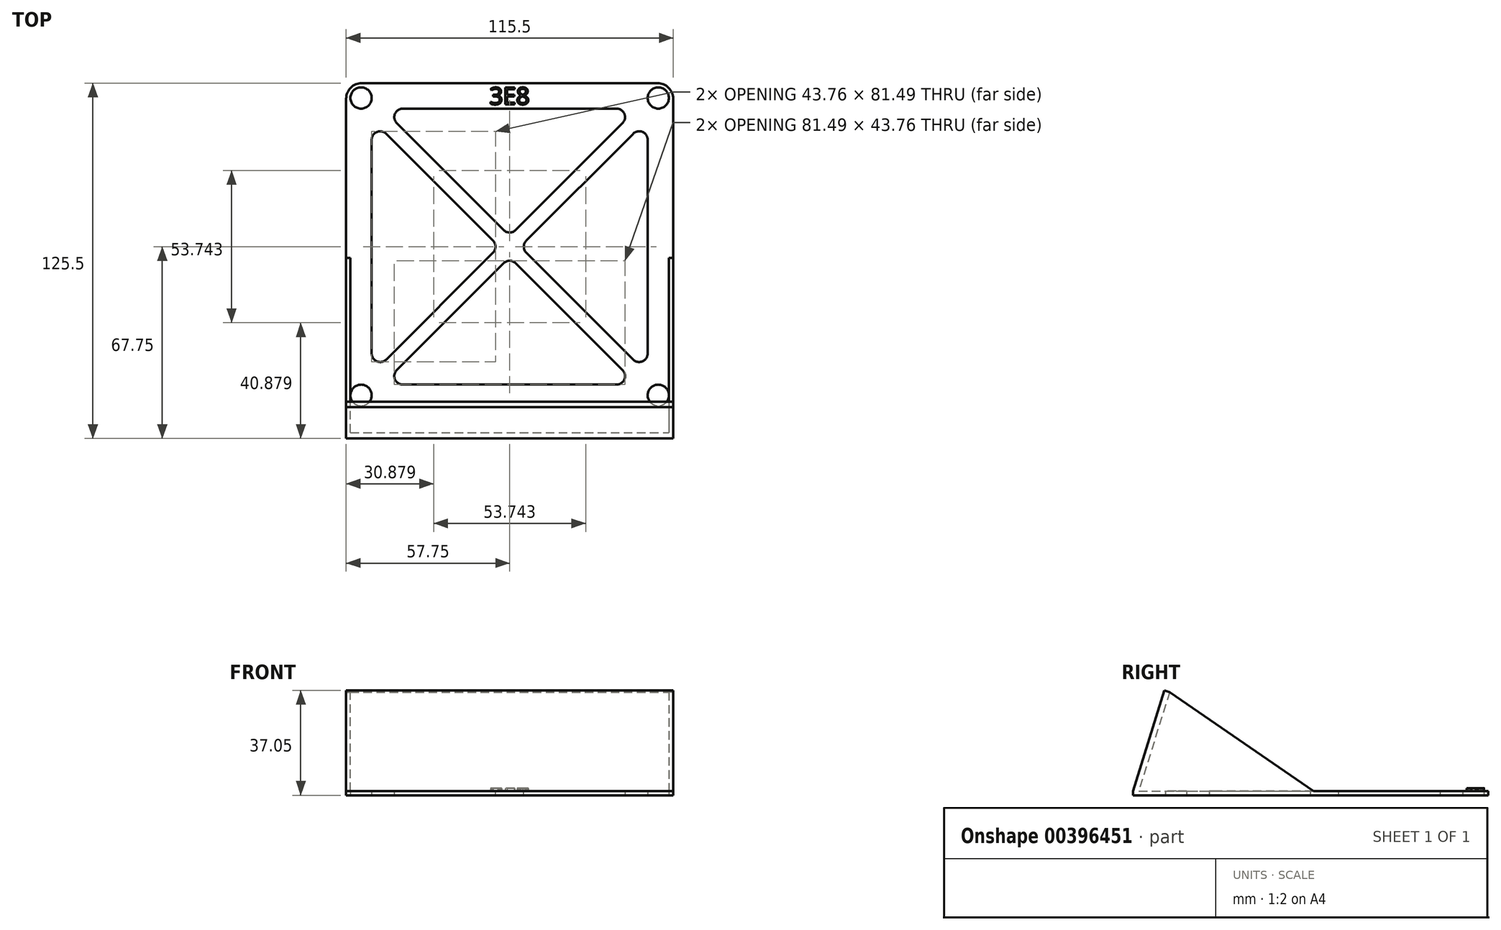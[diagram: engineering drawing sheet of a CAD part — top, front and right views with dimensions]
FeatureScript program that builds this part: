
annotation { "Feature Type Name" : "Feature", "Feature Type Description" : "" }
export const myFeature = defineFeature(function(context is Context, id is Id, definition is map)
    precondition{}
    {
        {
            assignVariable(context, id + "F0", {"name" : "HoleDiam", "anyValue" : 7.5});
        }
        {
            var Q0;
            Q0=qCreatedBy(makeId("Top.planeOp"),FACE);
            var sketch = newSketch(context, id + "F1", { "sketchPlane" : qUnion([Q0])});
            skLineSegment(sketch, "E0.bottom", {"start": v(52.5, -52.5) * mm, "end": v(-52.5, -52.5) * mm, "construction": true});
            skLineSegment(sketch, "E0.top", {"start": v(52.5, 52.5) * mm, "end": v(-52.5, 52.5) * mm, "construction": true});
            skLineSegment(sketch, "E0.left", {"start": v(52.5, -52.5) * mm, "end": v(52.5, 52.5) * mm, "construction": true});
            skLineSegment(sketch, "E0.right", {"start": v(-52.5, -52.5) * mm, "end": v(-52.5, 52.5) * mm, "construction": true});
            skPoint(sketch, "E0.middle", {"position": v(0, 0) * mm});
            skCircle(sketch, "E1", {"center": v(-52.5, 52.5) * mm, "radius": 3.75 * mm});
            skCircle(sketch, "E2", {"center": v(52.5, 52.5) * mm, "radius": 3.75 * mm});
            skCircle(sketch, "E3", {"center": v(52.5, -52.5) * mm, "radius": 3.75 * mm});
            skCircle(sketch, "E4", {"center": v(-52.5, -52.5) * mm, "radius": 3.75 * mm});
            skLineSegment(sketch, "E5.bottom", {"start": v(57.75, 57.75) * mm, "end": v(-57.75, 57.75) * mm});
            skLineSegment(sketch, "E5.top", {"start": v(57.75, -57.75) * mm, "end": v(-57.75, -57.75) * mm});
            skLineSegment(sketch, "E5.left", {"start": v(57.75, 57.75) * mm, "end": v(57.75, -57.75) * mm});
            skLineSegment(sketch, "E5.right", {"start": v(-57.75, 57.75) * mm, "end": v(-57.75, -57.75) * mm});
            skPoint(sketch, "E6.endSnap0", {"position": v(0, 52.5) * mm});
            skLineSegment(sketch, "E7", {"start": v(0, 52.5) * mm, "end": v(0, 48.75) * mm, "construction": true});
            skLineSegment(sketch, "E8", {"start": v(-45, 48.75) * mm, "end": v(45, 48.75) * mm});
            skLineSegment(sketch, "E9", {"start": v(-45, 48.75) * mm, "end": v(0, 3.75) * mm});
            skLineSegment(sketch, "E10", {"start": v(0, 3.75) * mm, "end": v(45, 48.75) * mm});
            skLineSegment(sketch, "E11.1.0", {"start": v(-48.75, -45) * mm, "end": v(-3.75, 0) * mm});
            skLineSegment(sketch, "E11.1.1", {"start": v(-48.75, -45) * mm, "end": v(-48.75, 45) * mm});
            skLineSegment(sketch, "E11.1.2", {"start": v(-3.75, 0) * mm, "end": v(-48.75, 45) * mm});
            skLineSegment(sketch, "E11.2.0", {"start": v(45, -48.75) * mm, "end": v(0, -3.75) * mm});
            skLineSegment(sketch, "E11.2.1", {"start": v(45, -48.75) * mm, "end": v(-45, -48.75) * mm});
            skLineSegment(sketch, "E11.2.2", {"start": v(0, -3.75) * mm, "end": v(-45, -48.75) * mm});
            skLineSegment(sketch, "E11.3.0", {"start": v(48.75, 45) * mm, "end": v(3.75, 0) * mm});
            skLineSegment(sketch, "E11.3.1", {"start": v(48.75, 45) * mm, "end": v(48.75, -45) * mm});
            skLineSegment(sketch, "E11.3.2", {"start": v(3.75, 0) * mm, "end": v(48.75, -45) * mm});
            skSolve(sketch);
        }
        {
            var Q0;
            Q0 = qSketchRegion(id + "F1", true);
            extrude(context, id + "F2", {"entities" : qUnion([Q0]), "depth" : 1.5 * mm});
        }
        {
            var Q0;
            Q0=makeQuery(id+"F2.opExtrude","SWEPT_FACE",FACE,{"disambiguationData":[OSD([sQuery(id+"F1.wireOp",EDGE,"E5.top")])]});
            extrude(context, id + "F3", {"entities" : qUnion([Q0]), "operationType" : NewBodyOperationType.ADD, "depth" : 10 * mm});
        }
        {
            var Q0;
            {var subQ0=sQuery(id+"F1.wireOp",EDGE,"E5.left");Q0=makeQuery(id+"F3.boolean.opBoolean","MERGE",FACE,{"derivedFrom":[makeQuery(id+"F2.opExtrude","SWEPT_FACE",FACE,{"disambiguationData":[OSD([subQ0])]}),makeQuery(id+"F3.opExtrude","SWEPT_FACE",FACE,{"disambiguationData":[OSD([sQuery(id+"F1.wireOp",EDGE,"E5.top"),subQ0])]})]});}
            var sketch = newSketch(context, id + "F4", { "sketchPlane" : qUnion([Q0])});
            skLineSegment(sketch, "E12", {"start": v(-67.75, 1.5) * mm, "end": v(-56.71, 37.05) * mm});
            skLineSegment(sketch, "E13", {"start": v(-56.71, 37.05) * mm, "end": v(-54.8, 36.45) * mm});
            skLineSegment(sketch, "E14", {"start": v(-54.8, 36.45) * mm, "end": v(-65.66, 1.5) * mm});
            skLineSegment(sketch, "E15", {"start": v(-65.66, 1.5) * mm, "end": v(-67.75, 1.5) * mm});
            skLineSegment(sketch, "E16", {"start": v(-54.8, 36.45) * mm, "end": v(57.75, 1.5) * mm, "construction": true});
            skSolve(sketch);
        }
        {
            var Q0;
            Q0 = qSketchRegion(id + "F4", true);
            var Q1;
            {var subQ0=sQuery(id+"F1.wireOp",EDGE,"E5.right");Q1=makeQuery(id+"F3.boolean.opBoolean","MERGE",FACE,{"derivedFrom":[makeQuery(id+"F2.opExtrude","SWEPT_FACE",FACE,{"disambiguationData":[OSD([subQ0])]}),makeQuery(id+"F3.opExtrude","SWEPT_FACE",FACE,{"disambiguationData":[OSD([sQuery(id+"F1.wireOp",EDGE,"E5.top"),subQ0])]})]});}
            extrude(context, id + "F5", {"entities" : qUnion([Q0]), "operationType" : NewBodyOperationType.ADD, "endBound" : BoundingType.UP_TO_SURFACE, "oppositeDirection" : true, "endBoundEntityFace" : qUnion([Q1]), "depth" : 25 * mm});
        }
        {
            var Q0;
            {var subQ0=sQuery(id+"F1.wireOp",EDGE,"E5.top");Q0=makeQuery(id+"F3.boolean.opBoolean","MERGE",FACE,{"derivedFrom":[makeQuery(id+"F2.opExtrude","CAP_FACE",FACE,{"disambiguationData":[OSD([sQuery(id+"F1.wireOp",EDGE,"E1"),sQuery(id+"F1.wireOp",EDGE,"E2"),sQuery(id+"F1.wireOp",EDGE,"E3"),sQuery(id+"F1.wireOp",EDGE,"E4"),sQuery(id+"F1.wireOp",EDGE,"E5.bottom"),subQ0,sQuery(id+"F1.wireOp",EDGE,"E5.left"),sQuery(id+"F1.wireOp",EDGE,"E5.right"),sQuery(id+"F1.wireOp",EDGE,"E8"),sQuery(id+"F1.wireOp",EDGE,"E9"),sQuery(id+"F1.wireOp",EDGE,"E10"),sQuery(id+"F1.wireOp",EDGE,"E11.1.0"),sQuery(id+"F1.wireOp",EDGE,"E11.1.1"),sQuery(id+"F1.wireOp",EDGE,"E11.1.2"),sQuery(id+"F1.wireOp",EDGE,"E11.2.0"),sQuery(id+"F1.wireOp",EDGE,"E11.2.1"),sQuery(id+"F1.wireOp",EDGE,"E11.2.2"),sQuery(id+"F1.wireOp",EDGE,"E11.3.0"),sQuery(id+"F1.wireOp",EDGE,"E11.3.1"),sQuery(id+"F1.wireOp",EDGE,"E11.3.2")])],"isStart":false}),makeQuery(id+"F3.opExtrude","SWEPT_FACE",FACE,{"disambiguationData":[OSD([subQ0]),TDD([makeQuery(id+"F2.opExtrude","CAP_EDGE",EDGE,{"disambiguationData":[OSD([subQ0])],"isStart":false})])]})]});}
            var sketch = newSketch(context, id + "F6", { "sketchPlane" : qUnion([Q0])});
            skPoint(sketch, "E17.0", {"position": v(-57.75, -65.66) * mm});
            skPoint(sketch, "E18.oppositeSnap0", {"position": v(-57.75, -3.95) * mm});
            skLineSegment(sketch, "E18.bottom", {"start": v(-57.75, -65.66) * mm, "end": v(-56.25, -65.66) * mm});
            skLineSegment(sketch, "E18.top", {"start": v(-57.75, -3.95) * mm, "end": v(-56.25, -3.95) * mm});
            skLineSegment(sketch, "E18.left", {"start": v(-57.75, -65.66) * mm, "end": v(-57.75, -3.95) * mm});
            skLineSegment(sketch, "E18.right", {"start": v(-56.25, -65.66) * mm, "end": v(-56.25, -3.95) * mm});
            skLineSegment(sketch, "E19", {"start": v(0, 0) * mm, "end": v(0, -48.75) * mm, "construction": true});
            skLineSegment(sketch, "E20.MirrorCS", {"start": v(56.25, -65.66) * mm, "end": v(56.25, -3.95) * mm});
            skLineSegment(sketch, "E21.MirrorCS", {"start": v(57.75, -3.95) * mm, "end": v(56.25, -3.95) * mm});
            skLineSegment(sketch, "E22.MirrorCS", {"start": v(57.75, -65.66) * mm, "end": v(57.75, -3.95) * mm});
            skLineSegment(sketch, "E23.MirrorCS", {"start": v(57.75, -65.66) * mm, "end": v(56.25, -65.66) * mm});
            skSolve(sketch);
        }
        {
            var Q0;
            Q0=makeQuery(id+"F5.opExtrude","SWEPT_FACE",FACE,{"disambiguationData":[OSD([sQuery(id+"F4.wireOp",EDGE,"E14")])]});
            var sketch = newSketch(context, id + "F7", { "sketchPlane" : qUnion([Q0])});
            skLineSegment(sketch, "E24", {"start": v(0, -18.04) * mm, "end": v(0, 18.56) * mm, "construction": true});
            skLineSegment(sketch, "E25.MirrorCS", {"start": v(-56.25, -18.04) * mm, "end": v(-56.25, 18.56) * mm});
            skLineSegment(sketch, "E26.MirrorCS", {"start": v(-57.75, 18.56) * mm, "end": v(-56.25, 18.56) * mm});
            skLineSegment(sketch, "E27.MirrorCS", {"start": v(-57.75, -18.04) * mm, "end": v(-57.75, 18.56) * mm});
            skLineSegment(sketch, "E28.MirrorCS", {"start": v(-57.75, -18.04) * mm, "end": v(-56.25, -18.04) * mm});
            skLineSegment(sketch, "E29.0", {"start": v(-57.75, -18.04) * mm, "end": v(-56.25, -18.04) * mm, "construction": true});
            skLineSegment(sketch, "E30.MirrorCS", {"start": v(56.25, -18.04) * mm, "end": v(56.25, 18.56) * mm});
            skLineSegment(sketch, "E31.MirrorCS", {"start": v(57.75, -18.04) * mm, "end": v(57.75, 18.56) * mm});
            skLineSegment(sketch, "E32.MirrorCS", {"start": v(57.75, -18.04) * mm, "end": v(56.25, -18.04) * mm});
            skLineSegment(sketch, "E33.MirrorCS", {"start": v(57.75, 18.56) * mm, "end": v(56.25, 18.56) * mm});
            skSolve(sketch);
        }
        {
            var Q0;
            Q0=sQuery(id+"F6.wireOp",VERTEX,"E18.right.end");
            var Q1;
            Q1=sQuery(id+"F7.wireOp",VERTEX,"E33.MirrorCS.start");
            var Q2;
            Q2=sQuery(id+"F6.wireOp",VERTEX,"E18.oppositeSnap0");
            cPlane(context, id + "F8", {"entities" : qUnion([Q0, Q1, Q2]), "cplaneType" : CPlaneType.THREE_POINT, "offset" : 25 * mm, "width" : 150 * mm, "height" : 150 * mm});
        }
        {
            var Q0;
            Q0=qCreatedBy(id+"F8.planeOp",FACE);
            var sketch = newSketch(context, id + "F9", { "sketchPlane" : qUnion([Q0])});
            skLineSegment(sketch, "E34.0", {"start": v(-57.75, -4.1) * mm, "end": v(-56.25, -4.1) * mm});
            skLineSegment(sketch, "E35.0", {"start": v(-57.75, -54.95) * mm, "end": v(-57.75, -4.1) * mm});
            skLineSegment(sketch, "E36.0", {"start": v(-56.25, -54.95) * mm, "end": v(-56.25, -4.1) * mm});
            skLineSegment(sketch, "E37.0", {"start": v(-57.75, -54.95) * mm, "end": v(-57.75, -65.81) * mm});
            skLineSegment(sketch, "E38.0", {"start": v(-56.25, -54.95) * mm, "end": v(-56.25, -65.81) * mm});
            skLineSegment(sketch, "E39.0", {"start": v(-57.75, -65.81) * mm, "end": v(-56.25, -65.81) * mm});
            skLineSegment(sketch, "E40.0", {"start": v(0, -0.85) * mm, "end": v(0, -41.02) * mm, "construction": true});
            skLineSegment(sketch, "E41.MirrorCS", {"start": v(57.75, -54.95) * mm, "end": v(57.75, -4.1) * mm});
            skLineSegment(sketch, "E42.MirrorCS", {"start": v(57.75, -4.1) * mm, "end": v(56.25, -4.1) * mm});
            skLineSegment(sketch, "E43.MirrorCS", {"start": v(56.25, -54.95) * mm, "end": v(56.25, -4.1) * mm});
            skLineSegment(sketch, "E44.MirrorCS", {"start": v(57.75, -54.95) * mm, "end": v(57.75, -65.81) * mm});
            skLineSegment(sketch, "E45.MirrorCS", {"start": v(56.25, -54.95) * mm, "end": v(56.25, -65.81) * mm});
            skLineSegment(sketch, "E46.MirrorCS", {"start": v(57.75, -65.81) * mm, "end": v(56.25, -65.81) * mm});
            skSolve(sketch);
        }
        {
            var Q0;
            Q0 = qSketchRegion(id + "F9", true);
            var Q1;
            Q1=makeQuery(id+"F2.opExtrude","SWEPT_BODY",BODY,{"disambiguationData":[OSD([sQuery(id+"F1.wireOp",EDGE,"E1"),sQuery(id+"F1.wireOp",EDGE,"E2"),sQuery(id+"F1.wireOp",EDGE,"E3"),sQuery(id+"F1.wireOp",EDGE,"E4"),sQuery(id+"F1.wireOp",EDGE,"E5.bottom"),sQuery(id+"F1.wireOp",EDGE,"E5.top"),sQuery(id+"F1.wireOp",EDGE,"E5.left"),sQuery(id+"F1.wireOp",EDGE,"E5.right"),sQuery(id+"F1.wireOp",EDGE,"E8"),sQuery(id+"F1.wireOp",EDGE,"E9"),sQuery(id+"F1.wireOp",EDGE,"E10"),sQuery(id+"F1.wireOp",EDGE,"E11.1.0"),sQuery(id+"F1.wireOp",EDGE,"E11.1.1"),sQuery(id+"F1.wireOp",EDGE,"E11.1.2"),sQuery(id+"F1.wireOp",EDGE,"E11.2.0"),sQuery(id+"F1.wireOp",EDGE,"E11.2.1"),sQuery(id+"F1.wireOp",EDGE,"E11.2.2"),sQuery(id+"F1.wireOp",EDGE,"E11.3.0"),sQuery(id+"F1.wireOp",EDGE,"E11.3.1"),sQuery(id+"F1.wireOp",EDGE,"E11.3.2")])]});
            extrude(context, id + "F10", {"entities" : qUnion([Q0]), "operationType" : NewBodyOperationType.ADD, "endBound" : BoundingType.UP_TO_BODY, "oppositeDirection" : true, "endBoundEntityBody" : qUnion([Q1]), "depth" : 25 * mm});
        }
        {
            var Q0;
            Q0=makeQuery(id+"F2.opExtrude","SWEPT_EDGE",EDGE,{"disambiguationData":[OSD([sQuery(id+"F1.wireOp",EDGE,"E11.2.0"),sQuery(id+"F1.wireOp",EDGE,"E11.2.2")])]});
            var Q1;
            Q1=makeQuery(id+"F2.opExtrude","SWEPT_EDGE",EDGE,{"disambiguationData":[OSD([sQuery(id+"F1.wireOp",EDGE,"E11.3.0"),sQuery(id+"F1.wireOp",EDGE,"E11.3.2")])]});
            var Q2;
            Q2=makeQuery(id+"F2.opExtrude","SWEPT_EDGE",EDGE,{"disambiguationData":[OSD([sQuery(id+"F1.wireOp",EDGE,"E9"),sQuery(id+"F1.wireOp",EDGE,"E10")])]});
            var Q3;
            Q3=makeQuery(id+"F2.opExtrude","SWEPT_EDGE",EDGE,{"disambiguationData":[OSD([sQuery(id+"F1.wireOp",EDGE,"E11.1.0"),sQuery(id+"F1.wireOp",EDGE,"E11.1.2")])]});
            var Q4;
            Q4=makeQuery(id+"F2.opExtrude","SWEPT_EDGE",EDGE,{"disambiguationData":[OSD([sQuery(id+"F1.wireOp",EDGE,"E11.2.0"),sQuery(id+"F1.wireOp",EDGE,"E11.2.1")])]});
            var Q5;
            Q5=makeQuery(id+"F2.opExtrude","SWEPT_EDGE",EDGE,{"disambiguationData":[OSD([sQuery(id+"F1.wireOp",EDGE,"E11.3.1"),sQuery(id+"F1.wireOp",EDGE,"E11.3.2")])]});
            var Q6;
            Q6=makeQuery(id+"F2.opExtrude","SWEPT_EDGE",EDGE,{"disambiguationData":[OSD([sQuery(id+"F1.wireOp",EDGE,"E11.2.1"),sQuery(id+"F1.wireOp",EDGE,"E11.2.2")])]});
            var Q7;
            Q7=makeQuery(id+"F2.opExtrude","SWEPT_EDGE",EDGE,{"disambiguationData":[OSD([sQuery(id+"F1.wireOp",EDGE,"E11.1.0"),sQuery(id+"F1.wireOp",EDGE,"E11.1.1")])]});
            var Q8;
            Q8=makeQuery(id+"F2.opExtrude","SWEPT_EDGE",EDGE,{"disambiguationData":[OSD([sQuery(id+"F1.wireOp",EDGE,"E11.1.1"),sQuery(id+"F1.wireOp",EDGE,"E11.1.2")])]});
            var Q9;
            Q9=makeQuery(id+"F2.opExtrude","SWEPT_EDGE",EDGE,{"disambiguationData":[OSD([sQuery(id+"F1.wireOp",EDGE,"E8"),sQuery(id+"F1.wireOp",EDGE,"E9")])]});
            var Q10;
            Q10=makeQuery(id+"F2.opExtrude","SWEPT_EDGE",EDGE,{"disambiguationData":[OSD([sQuery(id+"F1.wireOp",EDGE,"E8"),sQuery(id+"F1.wireOp",EDGE,"E10")])]});
            var Q11;
            Q11=makeQuery(id+"F2.opExtrude","SWEPT_EDGE",EDGE,{"disambiguationData":[OSD([sQuery(id+"F1.wireOp",EDGE,"E11.3.0"),sQuery(id+"F1.wireOp",EDGE,"E11.3.1")])]});
            var Q12;
            {var subQ0=sQuery(id+"F9.wireOp",EDGE,"E39.0");var subQ1=sQuery(id+"F9.wireOp",EDGE,"E38.0");var subQ2=sQuery(id+"F9.wireOp",EDGE,"E37.0");var subQ3=sQuery(id+"F9.wireOp",EDGE,"E36.0");var subQ4=sQuery(id+"F9.wireOp",EDGE,"E35.0");var subQ5=sQuery(id+"F9.wireOp",EDGE,"E34.0");var subQ6=sQuery(id+"F1.wireOp",EDGE,"E5.top");var subQ7=makeQuery(id+"F3.opExtrude","SWEPT_FACE",FACE,{"disambiguationData":[OSD([subQ6]),TDD([makeQuery(id+"F2.opExtrude","CAP_EDGE",EDGE,{"disambiguationData":[OSD([subQ6])],"isStart":false})])]});var subQ8=sQuery(id+"F1.wireOp",EDGE,"E4");var subQ10=makeQuery(id+"F2.opExtrude","CAP_FACE",FACE,{"disambiguationData":[OSD([sQuery(id+"F1.wireOp",EDGE,"E1"),sQuery(id+"F1.wireOp",EDGE,"E2"),sQuery(id+"F1.wireOp",EDGE,"E3"),subQ8,sQuery(id+"F1.wireOp",EDGE,"E5.bottom"),subQ6,sQuery(id+"F1.wireOp",EDGE,"E5.left"),sQuery(id+"F1.wireOp",EDGE,"E5.right"),sQuery(id+"F1.wireOp",EDGE,"E8"),sQuery(id+"F1.wireOp",EDGE,"E9"),sQuery(id+"F1.wireOp",EDGE,"E10"),sQuery(id+"F1.wireOp",EDGE,"E11.1.0"),sQuery(id+"F1.wireOp",EDGE,"E11.1.1"),sQuery(id+"F1.wireOp",EDGE,"E11.1.2"),sQuery(id+"F1.wireOp",EDGE,"E11.2.0"),sQuery(id+"F1.wireOp",EDGE,"E11.2.1"),sQuery(id+"F1.wireOp",EDGE,"E11.2.2"),sQuery(id+"F1.wireOp",EDGE,"E11.3.0"),sQuery(id+"F1.wireOp",EDGE,"E11.3.1"),sQuery(id+"F1.wireOp",EDGE,"E11.3.2")])],"isStart":false});var subQ12=makeQuery(id+"F10.opExtrude","CAP_EDGE",EDGE,{"disambiguationData":[OSD([subQ3,subQ1])],"isStart":false});Q12=qUnion([makeQuery(id+"F10.boolean.opBoolean","SPLIT",EDGE,{"disambiguationData":[TD([makeQuery(id+"F5.opExtrude","SWEPT_FACE",FACE,{"disambiguationData":[OSD([sQuery(id+"F4.wireOp",EDGE,"E14")])]})])],"derivedFrom":subQ12}),makeQuery(id+"F10.opExtrude","TWEAK_EDGE",EDGE,{"derivedFrom":[makeQuery(id+"F3.boolean.opBoolean","MERGE",FACE,{"derivedFrom":[subQ10,subQ7]}),makeQuery(id+"F9.imprint","IMPRINT",EDGE,{"derivedFrom":subQ5}),makeQuery(id+"F9.imprint","IMPRINT",EDGE,{"derivedFrom":subQ4}),makeQuery(id+"F9.imprint","IMPRINT",EDGE,{"derivedFrom":subQ3}),makeQuery(id+"F9.imprint","IMPRINT",EDGE,{"derivedFrom":subQ2}),makeQuery(id+"F9.imprint","IMPRINT",EDGE,{"derivedFrom":subQ1}),makeQuery(id+"F9.imprint","IMPRINT",EDGE,{"derivedFrom":subQ0})]}),makeQuery(id+"F10.boolean.opBoolean","SPLIT",EDGE,{"disambiguationData":[TD([makeQuery(id+"F10.opExtrude","CAP_FACE",FACE,{"disambiguationData":[OSD([subQ5,subQ4,subQ3,subQ2,subQ1,subQ0])],"isStart":true})])],"derivedFrom":subQ12})]);}
            var Q13;
            Q13=makeQuery(id+"F10.opExtrude","TWEAK_EDGE",EDGE,{"derivedFrom":[makeQuery(id+"F5.opExtrude","SWEPT_FACE",FACE,{"disambiguationData":[OSD([sQuery(id+"F4.wireOp",EDGE,"E14")])]}),makeQuery(id+"F9.imprint","IMPRINT",EDGE,{"derivedFrom":sQuery(id+"F9.wireOp",EDGE,"E36.0")}),makeQuery(id+"F9.imprint","IMPRINT",EDGE,{"derivedFrom":sQuery(id+"F9.wireOp",EDGE,"E38.0")})]});
            var Q14;
            Q14=makeQuery(id+"F5.opExtrude","SWEPT_EDGE",EDGE,{"disambiguationData":[OSD([sQuery(id+"F1.wireOp",EDGE,"E5.top"),sQuery(id+"F1.wireOp",EDGE,"E5.left"),sQuery(id+"F4.wireOp",EDGE,"E14"),sQuery(id+"F4.wireOp",EDGE,"E15")])]});
            var Q15;
            Q15=makeQuery(id+"F10.opExtrude","CAP_EDGE",EDGE,{"disambiguationData":[OSD([sQuery(id+"F9.wireOp",EDGE,"E42.MirrorCS")])],"isStart":false});
            var Q16;
            {var subQ0=sQuery(id+"F1.wireOp",EDGE,"E5.top");var subQ1=makeQuery(id+"F3.opExtrude","SWEPT_FACE",FACE,{"disambiguationData":[OSD([subQ0]),TDD([makeQuery(id+"F2.opExtrude","CAP_EDGE",EDGE,{"disambiguationData":[OSD([subQ0])],"isStart":false})])]});var subQ2=sQuery(id+"F1.wireOp",EDGE,"E3");var subQ3=sQuery(id+"F9.wireOp",EDGE,"E45.MirrorCS");var subQ4=sQuery(id+"F9.wireOp",EDGE,"E43.MirrorCS");var subQ5=makeQuery(id+"F2.opExtrude","CAP_FACE",FACE,{"disambiguationData":[OSD([sQuery(id+"F1.wireOp",EDGE,"E1"),sQuery(id+"F1.wireOp",EDGE,"E2"),subQ2,sQuery(id+"F1.wireOp",EDGE,"E4"),sQuery(id+"F1.wireOp",EDGE,"E5.bottom"),subQ0,sQuery(id+"F1.wireOp",EDGE,"E5.left"),sQuery(id+"F1.wireOp",EDGE,"E5.right"),sQuery(id+"F1.wireOp",EDGE,"E8"),sQuery(id+"F1.wireOp",EDGE,"E9"),sQuery(id+"F1.wireOp",EDGE,"E10"),sQuery(id+"F1.wireOp",EDGE,"E11.1.0"),sQuery(id+"F1.wireOp",EDGE,"E11.1.1"),sQuery(id+"F1.wireOp",EDGE,"E11.1.2"),sQuery(id+"F1.wireOp",EDGE,"E11.2.0"),sQuery(id+"F1.wireOp",EDGE,"E11.2.1"),sQuery(id+"F1.wireOp",EDGE,"E11.2.2"),sQuery(id+"F1.wireOp",EDGE,"E11.3.0"),sQuery(id+"F1.wireOp",EDGE,"E11.3.1"),sQuery(id+"F1.wireOp",EDGE,"E11.3.2")])],"isStart":false});Q16=makeQuery(id+"F10.boolean.opBoolean","SPLIT",EDGE,{"disambiguationData":[TD([makeQuery(id+"F10.opExtrude","CAP_FACE",FACE,{"disambiguationData":[OSD([sQuery(id+"F9.wireOp",EDGE,"E41.MirrorCS"),sQuery(id+"F9.wireOp",EDGE,"E42.MirrorCS"),subQ4,sQuery(id+"F9.wireOp",EDGE,"E44.MirrorCS"),subQ3,sQuery(id+"F9.wireOp",EDGE,"E46.MirrorCS")])],"isStart":true})])],"derivedFrom":makeQuery(id+"F10.opExtrude","TWEAK_EDGE",EDGE,{"derivedFrom":[makeQuery(id+"F3.boolean.opBoolean","MERGE",FACE,{"derivedFrom":[subQ5,subQ1]}),makeQuery(id+"F9.imprint","IMPRINT",EDGE,{"derivedFrom":subQ4}),makeQuery(id+"F9.imprint","IMPRINT",EDGE,{"derivedFrom":subQ3})]})});}
            var Q17;
            Q17=makeQuery(id+"F10.opExtrude","CAP_EDGE",EDGE,{"disambiguationData":[OSD([sQuery(id+"F9.wireOp",EDGE,"E43.MirrorCS"),sQuery(id+"F9.wireOp",EDGE,"E45.MirrorCS")])],"isStart":false});
            fillet(context, id + "F11", {"entities" : qUnion([Q0, Q1, Q2, Q3, Q4, Q5, Q6, Q7, Q8, Q9, Q10, Q11, Q12, Q13, Q14, Q15, Q16, Q17]), "radius" : 3 * mm, "tangentPropagation" : true, "allowEdgeOverflow" : false});
        }
        {
            var Q0;
            Q0=makeQuery(id+"F2.opExtrude","SWEPT_EDGE",EDGE,{"disambiguationData":[OSD([sQuery(id+"F1.wireOp",EDGE,"E5.bottom"),sQuery(id+"F1.wireOp",EDGE,"E5.right")])]});
            var Q1;
            Q1=makeQuery(id+"F2.opExtrude","SWEPT_EDGE",EDGE,{"disambiguationData":[OSD([sQuery(id+"F1.wireOp",EDGE,"E5.bottom"),sQuery(id+"F1.wireOp",EDGE,"E5.left")])]});
            fillet(context, id + "F12", {"entities" : qUnion([Q0, Q1]), "radius" : (getVariable(context, 'HoleDiam') - 2) * mm, "tangentPropagation" : true, "allowEdgeOverflow" : false});
        }
        {
            var Q0;
            {var subQ0=sQuery(id+"F1.wireOp",EDGE,"E5.top");Q0=makeQuery(id+"F3.boolean.opBoolean","MERGE",FACE,{"derivedFrom":[makeQuery(id+"F2.opExtrude","CAP_FACE",FACE,{"disambiguationData":[OSD([sQuery(id+"F1.wireOp",EDGE,"E1"),sQuery(id+"F1.wireOp",EDGE,"E2"),sQuery(id+"F1.wireOp",EDGE,"E3"),sQuery(id+"F1.wireOp",EDGE,"E4"),sQuery(id+"F1.wireOp",EDGE,"E5.bottom"),subQ0,sQuery(id+"F1.wireOp",EDGE,"E5.left"),sQuery(id+"F1.wireOp",EDGE,"E5.right"),sQuery(id+"F1.wireOp",EDGE,"E8"),sQuery(id+"F1.wireOp",EDGE,"E9"),sQuery(id+"F1.wireOp",EDGE,"E10"),sQuery(id+"F1.wireOp",EDGE,"E11.1.0"),sQuery(id+"F1.wireOp",EDGE,"E11.1.1"),sQuery(id+"F1.wireOp",EDGE,"E11.1.2"),sQuery(id+"F1.wireOp",EDGE,"E11.2.0"),sQuery(id+"F1.wireOp",EDGE,"E11.2.1"),sQuery(id+"F1.wireOp",EDGE,"E11.2.2"),sQuery(id+"F1.wireOp",EDGE,"E11.3.0"),sQuery(id+"F1.wireOp",EDGE,"E11.3.1"),sQuery(id+"F1.wireOp",EDGE,"E11.3.2")])],"isStart":false}),makeQuery(id+"F3.opExtrude","SWEPT_FACE",FACE,{"disambiguationData":[OSD([subQ0]),TDD([makeQuery(id+"F2.opExtrude","CAP_EDGE",EDGE,{"disambiguationData":[OSD([subQ0])],"isStart":false})])]})]});}
            var sketch = newSketch(context, id + "F13", { "sketchPlane" : qUnion([Q0])});
            skText(sketch, "E47", { "text": "3E8", "fontName": "OpenSans-Regular.ttf"});
            skLineSegment(sketch, "E48", {"start": v(0, 57.75) * mm, "end": v(0, 48.75) * mm, "construction": true});
            skPoint(sketch, "E49", {"position": v(0, 53.25) * mm});
            const initialGuessF13  = {"E47": [-0.00714, 0.05025, 1, 0, 0.006]};
            skSetInitialGuess(sketch, initialGuessF13);
            skSolve(sketch);
        }
        {
            var Q0;
            Q0 = qSketchRegion(id + "F13", true);
            extrude(context, id + "F14", {"entities" : qUnion([Q0]), "operationType" : NewBodyOperationType.ADD, "depth" : 1 * mm});
        }
    });
